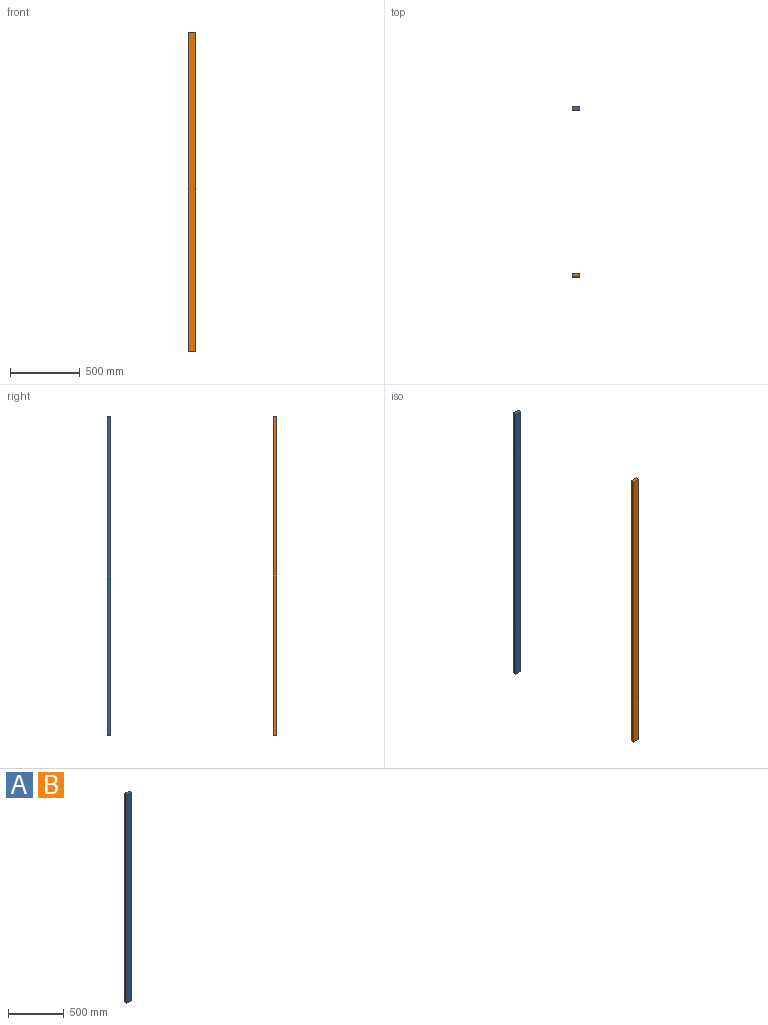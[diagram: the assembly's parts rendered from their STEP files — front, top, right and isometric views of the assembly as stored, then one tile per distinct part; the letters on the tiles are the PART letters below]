
ASSEMBLY  parts=2 mates=1
PART A: 6 faces, bbox 50.8x25.4x2286 mm
  f0: plane 2286x25.4mm, normal (-1,0,0), area 58064.4mm2, adj f1,f3,f4,f5
  f1: plane 50.8x25.4mm, normal (0,0,-1), area 1290.3mm2, adj f0,f2,f4,f5
  f2: plane 2286x25.4mm, normal (1,0,0), area 58064.4mm2, adj f1,f3,f4,f5
  f3: plane 50.8x25.4mm, normal (0,0,1), area 1290.3mm2, adj f0,f2,f4,f5
  f4: plane 2286x50.8mm, normal (0,-1,0), area 116128.8mm2, adj f0,f1,f2,f3
  f5: plane 2286x50.8mm, normal (0,1,0), area 116128.8mm2, adj f0,f1,f2,f3
PART B: same geometry as A
PLACE A at identity
PLACE B t=(0,-1193.8,0)mm
MATE parallel A.f5 <-> B.f4  axis (0,1,0) through (25.4,0,1143)mm
